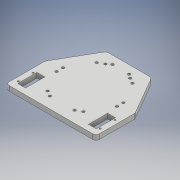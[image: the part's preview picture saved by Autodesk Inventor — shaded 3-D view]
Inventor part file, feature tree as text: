
AUTODESK INVENTOR PART (.ipt)
format: ipt  version: 2018 (Build 220112000, 112)  size: 201,216 bytes
history: native  units: mm
features: extrude x3, sketch x3, projected_geometry x2, fillet x1
ambient origin geometry x8: Origin, YZ Plane, XZ Plane, XY Plane, X Axis, Y Axis, Z Axis, Center Point
bodies: Solid1 (feature_tree)
feature tree (9):
  extrude  "Extrusion1"  TaperAngle=120.0deg  [1 undecoded]
  extrude  "Extrusion2"  Depth=47.462522mm
  extrude  "Extrusion3"  Depth=6.0mm TaperAngle=0.0deg
  fillet  "Fillet1"  Radius=2.02mm
  sketch  "Sketch1"  dims[d2=54.805mm d3=120.0deg]
  sketch  "Sketch2"  dims[d4=120.0deg d5=47.462522mm]
  projected_geometry  "Projected Loop1"
  sketch  "Sketch3"  dims[d6=47.462522mm d8=6.0mm d9=0.0mm d10=2.02mm d11=3.2mm d12=5.0mm d13=5.0mm d14=18.0mm d15=10.0mm d16=23.39mm d17=9.57mm d19=2.0mm d20=2.0mm d21=20.385mm d22=10.0mm d23=3.861382mm d24=6.0mm d25=0.0mm d26=3.1mm d27=39.0mm d28=4.5mm d29=4.5mm d30=4.5mm d31=4.5mm d32=4.5mm d33=4.5mm d34=4.5mm d35=4.5mm d36=4.5mm d37=4.5mm d38=10.0mm d39=0.0mm d40=59.755753mm d41=4.0mm]
  projected_geometry  "Projected Loop2"
note: 1 required parameter value undecoded (feature->parameter linkage not recoverable at this tier; creation-order binding heuristic only, values carry confidence <= 0.55)
